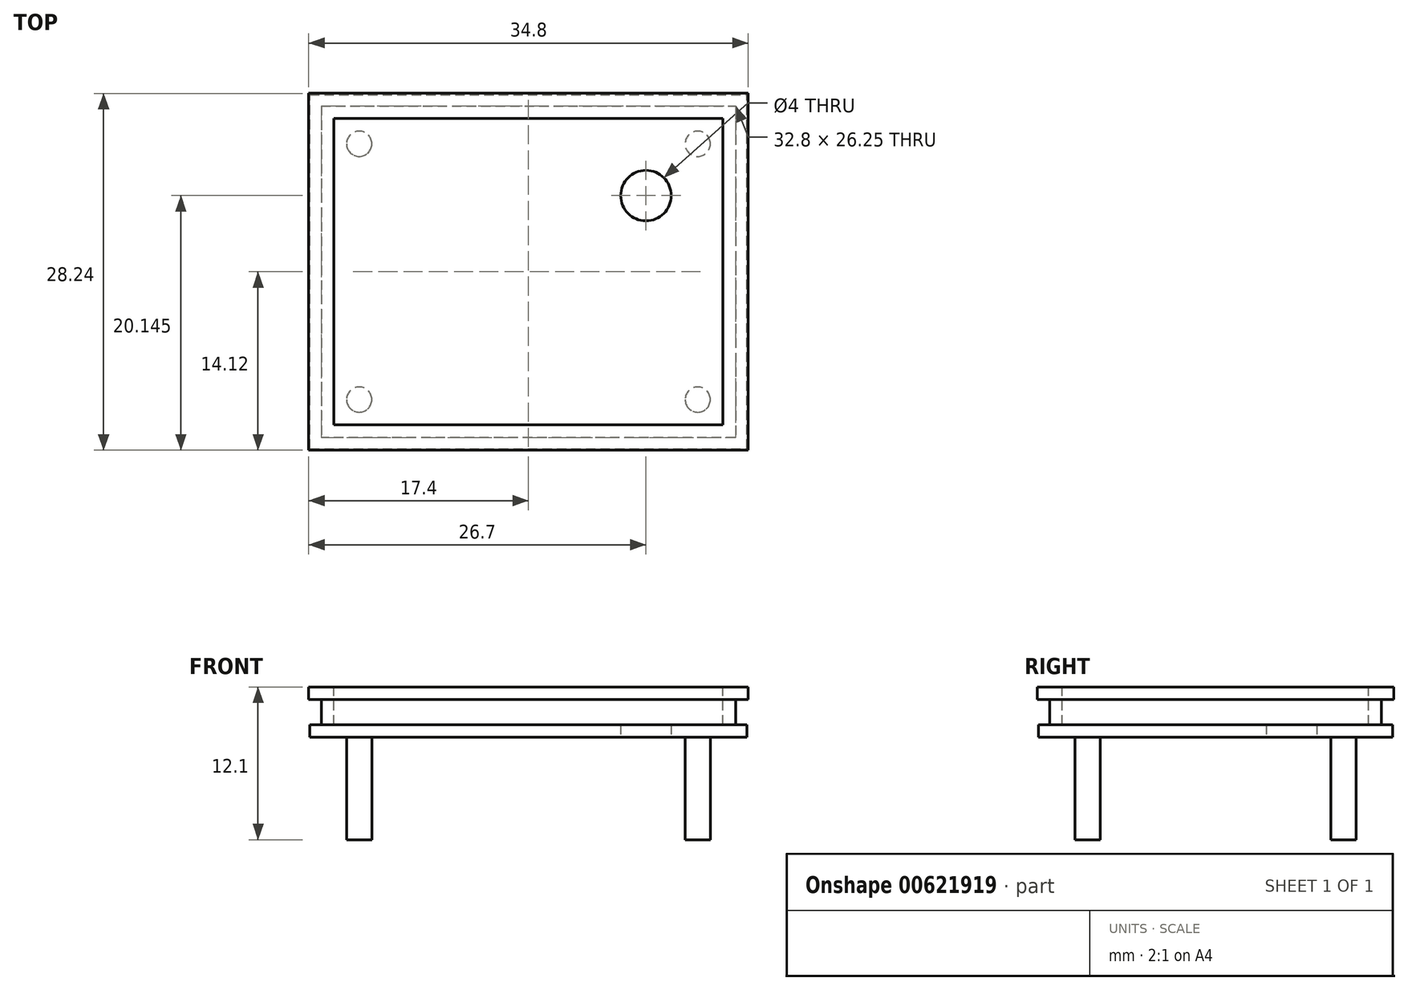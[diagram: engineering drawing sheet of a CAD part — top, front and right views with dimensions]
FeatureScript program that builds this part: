
annotation { "Feature Type Name" : "Feature", "Feature Type Description" : "" }
export const myFeature = defineFeature(function(context is Context, id is Id, definition is map)
    precondition{}
    {
        {
            var Q0;
            Q0=qCreatedBy(makeId("Top.planeOp"),FACE);
            var sketch = newSketch(context, id + "F0", { "sketchPlane" : qUnion([Q0])});
            skLineSegment(sketch, "E0.bottom", {"start": v(-17.4, -14.12) * mm, "end": v(17.4, -14.12) * mm});
            skLineSegment(sketch, "E0.top", {"start": v(-17.4, 14.13) * mm, "end": v(17.4, 14.13) * mm});
            skLineSegment(sketch, "E0.left", {"start": v(-17.4, -14.12) * mm, "end": v(-17.4, 14.13) * mm});
            skLineSegment(sketch, "E0.right", {"start": v(17.4, -14.12) * mm, "end": v(17.4, 14.13) * mm});
            skLineSegment(sketch, "E1", {"start": v(-17.4, 14.13) * mm, "end": v(17.4, -14.12) * mm});
            skLineSegment(sketch, "E2", {"start": v(17.4, 14.12) * mm, "end": v(-17.4, -14.12) * mm});
            skSolve(sketch);
        }
        {
            var Q0;
            {var subQ0=sQuery(id+"F0.wireOp",EDGE,"E0.left");Q0=makeQuery(id+"F0.imprint","IMPRINT",FACE,{"disambiguationData":[TD([[makeQuery(id+"F0.imprint","IMPRINT",EDGE,{"derivedFrom":subQ0}),-1.0]])]});}
            var Q1;
            {var subQ0=sQuery(id+"F0.wireOp",EDGE,"E0.bottom");Q1=makeQuery(id+"F0.imprint","IMPRINT",FACE,{"disambiguationData":[TD([[makeQuery(id+"F0.imprint","IMPRINT",EDGE,{"derivedFrom":subQ0}),1.0]])]});}
            var Q2;
            {var subQ0=sQuery(id+"F0.wireOp",EDGE,"E0.right");Q2=makeQuery(id+"F0.imprint","IMPRINT",FACE,{"disambiguationData":[TD([[makeQuery(id+"F0.imprint","IMPRINT",EDGE,{"derivedFrom":subQ0}),1.0]])]});}
            var Q3;
            {var subQ0=sQuery(id+"F0.wireOp",EDGE,"E0.top");Q3=makeQuery(id+"F0.imprint","IMPRINT",FACE,{"disambiguationData":[TD([[makeQuery(id+"F0.imprint","IMPRINT",EDGE,{"derivedFrom":subQ0}),-1.0]])]});}
            extrude(context, id + "F1", {"entities" : qUnion([Q0, Q1, Q2, Q3]), "depth" : 2.5 * mm, "offsetDistance" : 25 * mm});
        }
        {
            var Q0;
            Q0=makeQuery(id+"F1.opExtrude","CAP_FACE",FACE,{"disambiguationData":[OSD([sQuery(id+"F0.wireOp",EDGE,"E0.bottom"),sQuery(id+"F0.wireOp",EDGE,"E0.top"),sQuery(id+"F0.wireOp",EDGE,"E0.left"),sQuery(id+"F0.wireOp",EDGE,"E0.right")])],"isStart":false});
            var sketch = newSketch(context, id + "F2", { "sketchPlane" : qUnion([Q0])});
            skLineSegment(sketch, "E3.bottom", {"start": v(-15.4, -12.12) * mm, "end": v(15.4, -12.12) * mm});
            skLineSegment(sketch, "E3.top", {"start": v(-15.4, 12.13) * mm, "end": v(15.4, 12.13) * mm});
            skLineSegment(sketch, "E3.left", {"start": v(-15.4, -12.12) * mm, "end": v(-15.4, 12.13) * mm});
            skLineSegment(sketch, "E3.right", {"start": v(15.4, -12.12) * mm, "end": v(15.4, 12.13) * mm});
            skSolve(sketch);
        }
        {
            var Q0;
            Q0=makeQuery(id+"F2.imprint","IMPRINT",FACE,{"disambiguationData":[TD([[makeQuery(id+"F2.imprint","IMPRINT",EDGE,{"derivedFrom":sQuery(id+"F2.wireOp",EDGE,"E3.bottom")}),1.0]])]});
            extrude(context, id + "F3", {"entities" : qUnion([Q0]), "operationType" : NewBodyOperationType.REMOVE, "oppositeDirection" : true, "depth" : 1.5 * mm, "offsetDistance" : 25 * mm});
        }
        {
            var Q0;
            Q0=makeQuery(id+"F1.opExtrude","CAP_FACE",FACE,{"disambiguationData":[OSD([sQuery(id+"F0.wireOp",EDGE,"E0.bottom"),sQuery(id+"F0.wireOp",EDGE,"E0.top"),sQuery(id+"F0.wireOp",EDGE,"E0.left"),sQuery(id+"F0.wireOp",EDGE,"E0.right")])],"isStart":false});
            extrude(context, id + "F4", {"entities" : qUnion([Q0]), "operationType" : NewBodyOperationType.ADD, "depth" : 1.5 * mm, "offsetDistance" : 25 * mm});
        }
        {
            var Q0;
            {var subQ0=sQuery(id+"F0.wireOp",EDGE,"E0.bottom");Q0=makeQuery(id+"F4.boolean.opBoolean","MERGE",FACE,{"derivedFrom":[makeQuery(id+"F1.opExtrude","SWEPT_FACE",FACE,{"disambiguationData":[OSD([subQ0])]}),makeQuery(id+"F4.opExtrude","SWEPT_FACE",FACE,{"disambiguationData":[OSD([subQ0])]})]});}
            var sketch = newSketch(context, id + "F5", { "sketchPlane" : qUnion([Q0])});
            skLineSegment(sketch, "E4.bottom", {"start": v(-17.4, 3) * mm, "end": v(-16.4, 3) * mm});
            skLineSegment(sketch, "E4.top", {"start": v(-17.4, 1) * mm, "end": v(-16.4, 1) * mm});
            skLineSegment(sketch, "E4.left", {"start": v(-17.4, 3) * mm, "end": v(-17.4, 1) * mm});
            skLineSegment(sketch, "E4.right", {"start": v(-16.4, 3) * mm, "end": v(-16.4, 1) * mm});
            skSolve(sketch);
        }
        {
            var Q0;
            Q0=makeQuery(id+"F5.imprint","IMPRINT",FACE,{"disambiguationData":[TD([[makeQuery(id+"F5.imprint","IMPRINT",EDGE,{"derivedFrom":sQuery(id+"F5.wireOp",EDGE,"E4.bottom")}),-1.0]])]});
            extrude(context, id + "F6", {"entities" : qUnion([Q0]), "operationType" : NewBodyOperationType.REMOVE, "endBound" : BoundingType.THROUGH_ALL, "oppositeDirection" : true, "depth" : 25 * mm, "offsetDistance" : 25 * mm});
        }
        {
            var Q0;
            {var subQ0=sQuery(id+"F0.wireOp",EDGE,"E0.bottom");Q0=makeQuery(id+"F4.boolean.opBoolean","MERGE",FACE,{"derivedFrom":[makeQuery(id+"F1.opExtrude","SWEPT_FACE",FACE,{"disambiguationData":[OSD([subQ0])]}),makeQuery(id+"F4.opExtrude","SWEPT_FACE",FACE,{"disambiguationData":[OSD([subQ0])]})]});}
            var sketch = newSketch(context, id + "F7", { "sketchPlane" : qUnion([Q0])});
            skLineSegment(sketch, "E5.bottom", {"start": v(17.4, 3) * mm, "end": v(16.4, 3) * mm});
            skLineSegment(sketch, "E5.top", {"start": v(17.4, 1) * mm, "end": v(16.4, 1) * mm});
            skLineSegment(sketch, "E5.left", {"start": v(17.4, 3) * mm, "end": v(17.4, 1) * mm});
            skLineSegment(sketch, "E5.right", {"start": v(16.4, 3) * mm, "end": v(16.4, 1) * mm});
            skSolve(sketch);
        }
        {
            var Q0;
            Q0=makeQuery(id+"F7.imprint","IMPRINT",FACE,{"disambiguationData":[TD([[makeQuery(id+"F7.imprint","IMPRINT",EDGE,{"derivedFrom":sQuery(id+"F7.wireOp",EDGE,"E5.bottom")}),1.0]])]});
            extrude(context, id + "F8", {"entities" : qUnion([Q0]), "operationType" : NewBodyOperationType.REMOVE, "endBound" : BoundingType.THROUGH_ALL, "oppositeDirection" : true, "depth" : 25 * mm, "offsetDistance" : 25 * mm});
        }
        {
            var Q0;
            Q0=makeQuery(id+"F6.boolean.opBoolean","COPY",FACE,{"derivedFrom":makeQuery(id+"F6.opExtrude","SWEPT_FACE",FACE,{"disambiguationData":[OSD([sQuery(id+"F5.wireOp",EDGE,"E4.right")])]})});
            var sketch = newSketch(context, id + "F9", { "sketchPlane" : qUnion([Q0])});
            skLineSegment(sketch, "E6.bottom", {"start": v(13.12, 3) * mm, "end": v(14.12, 3) * mm});
            skLineSegment(sketch, "E6.top", {"start": v(13.12, 1) * mm, "end": v(14.12, 1) * mm});
            skLineSegment(sketch, "E6.left", {"start": v(13.12, 3) * mm, "end": v(13.12, 1) * mm});
            skLineSegment(sketch, "E6.right", {"start": v(14.12, 3) * mm, "end": v(14.12, 1) * mm});
            skSolve(sketch);
        }
        {
            var Q0;
            Q0=makeQuery(id+"F9.imprint","IMPRINT",FACE,{"disambiguationData":[TD([[makeQuery(id+"F9.imprint","IMPRINT",EDGE,{"derivedFrom":sQuery(id+"F9.wireOp",EDGE,"E6.bottom")}),-1.0]])]});
            extrude(context, id + "F10", {"entities" : qUnion([Q0]), "operationType" : NewBodyOperationType.REMOVE, "endBound" : BoundingType.THROUGH_ALL, "oppositeDirection" : true, "depth" : 25 * mm, "offsetDistance" : 25 * mm});
        }
        {
            var Q0;
            Q0=makeQuery(id+"F8.boolean.opBoolean","COPY",FACE,{"derivedFrom":makeQuery(id+"F8.opExtrude","SWEPT_FACE",FACE,{"disambiguationData":[OSD([sQuery(id+"F7.wireOp",EDGE,"E5.right")])]})});
            var sketch = newSketch(context, id + "F11", { "sketchPlane" : qUnion([Q0])});
            skLineSegment(sketch, "E7.bottom", {"start": v(14.13, 3) * mm, "end": v(13.13, 3) * mm});
            skLineSegment(sketch, "E7.top", {"start": v(14.13, 1) * mm, "end": v(13.13, 1) * mm});
            skLineSegment(sketch, "E7.left", {"start": v(14.13, 3) * mm, "end": v(14.13, 1) * mm});
            skLineSegment(sketch, "E7.right", {"start": v(13.13, 3) * mm, "end": v(13.13, 1) * mm});
            skSolve(sketch);
        }
        {
            var Q0;
            Q0=makeQuery(id+"F11.imprint","IMPRINT",FACE,{"disambiguationData":[TD([[makeQuery(id+"F11.imprint","IMPRINT",EDGE,{"derivedFrom":sQuery(id+"F11.wireOp",EDGE,"E7.bottom")}),1.0]])]});
            extrude(context, id + "F12", {"entities" : qUnion([Q0]), "operationType" : NewBodyOperationType.REMOVE, "endBound" : BoundingType.THROUGH_ALL, "oppositeDirection" : true, "depth" : 25 * mm, "offsetDistance" : 25 * mm});
        }
        {
            var Q0;
            Q0=makeQuery(id+"F1.opExtrude","CAP_FACE",FACE,{"disambiguationData":[OSD([sQuery(id+"F0.wireOp",EDGE,"E0.bottom"),sQuery(id+"F0.wireOp",EDGE,"E0.top"),sQuery(id+"F0.wireOp",EDGE,"E0.left"),sQuery(id+"F0.wireOp",EDGE,"E0.right")])],"isStart":true});
            var sketch = newSketch(context, id + "F13", { "sketchPlane" : qUnion([Q0])});
            skCircle(sketch, "E8", {"center": v(13.4, -10.13) * mm, "radius": 1 * mm});
            skSolve(sketch);
        }
        {
            var Q0;
            Q0=makeQuery(id+"F13.imprint","IMPRINT",FACE,{"disambiguationData":[TD([[makeQuery(id+"F13.imprint","IMPRINT",EDGE,{"derivedFrom":sQuery(id+"F13.wireOp",EDGE,"E8")}),-1.0]])]});
            var sketch = newSketch(context, id + "F14", { "sketchPlane" : qUnion([Q0])});
            skCircle(sketch, "E9", {"center": v(-13.4, -10.13) * mm, "radius": 1 * mm});
            skSolve(sketch);
        }
        {
            var Q0;
            Q0=makeQuery(id+"F14.imprint","IMPRINT",FACE,{"disambiguationData":[TD([[makeQuery(id+"F14.imprint","IMPRINT",EDGE,{"derivedFrom":sQuery(id+"F14.wireOp",EDGE,"E9")}),-1.0]])]});
            var sketch = newSketch(context, id + "F15", { "sketchPlane" : qUnion([Q0])});
            skCircle(sketch, "E10", {"center": v(-13.4, 10.12) * mm, "radius": 1 * mm});
            skSolve(sketch);
        }
        {
            var Q0;
            Q0=makeQuery(id+"F13.imprint","IMPRINT",FACE,{"disambiguationData":[TD([[makeQuery(id+"F13.imprint","IMPRINT",EDGE,{"derivedFrom":sQuery(id+"F13.wireOp",EDGE,"E8")}),-1.0]])]});
            var sketch = newSketch(context, id + "F16", { "sketchPlane" : qUnion([Q0])});
            skCircle(sketch, "E11", {"center": v(13.4, 10.12) * mm, "radius": 1 * mm});
            skSolve(sketch);
        }
        {
            var Q0;
            Q0=makeQuery(id+"F15.imprint","IMPRINT",FACE,{"disambiguationData":[TD([[makeQuery(id+"F15.imprint","IMPRINT",EDGE,{"derivedFrom":makeQuery(id+"F14.imprint","IMPRINT",EDGE,{"derivedFrom":sQuery(id+"F14.wireOp",EDGE,"E9")})}),1.0]])]});
            var Q1;
            Q1=makeQuery(id+"F13.imprint","IMPRINT",FACE,{"disambiguationData":[TD([[makeQuery(id+"F13.imprint","IMPRINT",EDGE,{"derivedFrom":sQuery(id+"F13.wireOp",EDGE,"E8")}),1.0]])]});
            var Q2;
            Q2=makeQuery(id+"F15.imprint","IMPRINT",FACE,{"disambiguationData":[TD([[makeQuery(id+"F15.imprint","IMPRINT",EDGE,{"derivedFrom":sQuery(id+"F15.wireOp",EDGE,"E10")}),1.0]])]});
            var Q3;
            Q3=makeQuery(id+"F16.imprint","IMPRINT",FACE,{"disambiguationData":[TD([[makeQuery(id+"F16.imprint","IMPRINT",EDGE,{"derivedFrom":sQuery(id+"F16.wireOp",EDGE,"E11")}),1.0]])]});
            extrude(context, id + "F17", {"entities" : qUnion([Q0, Q1, Q2, Q3]), "operationType" : NewBodyOperationType.ADD, "depth" : 8.1 * mm, "offsetDistance" : 25 * mm});
        }
        {
            var Q0;
            Q0=makeQuery(id+"F14.imprint","IMPRINT",FACE,{"disambiguationData":[TD([[makeQuery(id+"F14.imprint","IMPRINT",EDGE,{"derivedFrom":sQuery(id+"F14.wireOp",EDGE,"E9")}),-1.0]])]});
            var sketch = newSketch(context, id + "F18", { "sketchPlane" : qUnion([Q0])});
            skLineSegment(sketch, "E12.bottom", {"start": v(17.4, -14.13) * mm, "end": v(-17.4, -14.13) * mm});
            skLineSegment(sketch, "E12.top", {"start": v(17.4, 14.12) * mm, "end": v(-17.4, 14.12) * mm});
            skLineSegment(sketch, "E12.left", {"start": v(17.4, -14.13) * mm, "end": v(17.4, 14.12) * mm});
            skLineSegment(sketch, "E12.right", {"start": v(-17.4, -14.13) * mm, "end": v(-17.4, 14.12) * mm});
            skLineSegment(sketch, "E13.bottom", {"start": v(17.3, -14.03) * mm, "end": v(-17.3, -14.03) * mm});
            skLineSegment(sketch, "E13.top", {"start": v(17.3, 14.03) * mm, "end": v(-17.3, 14.02) * mm});
            skLineSegment(sketch, "E13.left", {"start": v(17.3, -14.03) * mm, "end": v(17.3, 14.03) * mm});
            skLineSegment(sketch, "E13.right", {"start": v(-17.3, -14.03) * mm, "end": v(-17.3, 14.02) * mm});
            skSolve(sketch);
        }
        {
            var Q0;
            Q0=makeQuery(id+"F18.imprint","IMPRINT",FACE,{"disambiguationData":[TD([[makeQuery(id+"F18.imprint","IMPRINT",EDGE,{"derivedFrom":sQuery(id+"F18.wireOp",EDGE,"E12.bottom")}),1.0]])]});
            var Q1;
            Q1=makeQuery(id+"F12.boolean.opBoolean","MERGE",FACE,{"derivedFrom":[makeQuery(id+"F10.boolean.opBoolean","MERGE",FACE,{"derivedFrom":[makeQuery(id+"F6.boolean.opBoolean","COPY",FACE,{"derivedFrom":makeQuery(id+"F6.opExtrude","SWEPT_FACE",FACE,{"disambiguationData":[OSD([sQuery(id+"F5.wireOp",EDGE,"E4.top")])]})}),makeQuery(id+"F8.boolean.opBoolean","COPY",FACE,{"derivedFrom":makeQuery(id+"F8.opExtrude","SWEPT_FACE",FACE,{"disambiguationData":[OSD([sQuery(id+"F7.wireOp",EDGE,"E5.top")])]})}),makeQuery(id+"F10.opExtrude","SWEPT_FACE",FACE,{"disambiguationData":[OSD([sQuery(id+"F9.wireOp",EDGE,"E6.top")])]})]}),makeQuery(id+"F12.opExtrude","SWEPT_FACE",FACE,{"disambiguationData":[OSD([sQuery(id+"F11.wireOp",EDGE,"E7.top")])]})]});
            extrude(context, id + "F19", {"entities" : qUnion([Q0]), "operationType" : NewBodyOperationType.REMOVE, "endBound" : BoundingType.UP_TO_SURFACE, "oppositeDirection" : true, "depth" : 25 * mm, "endBoundEntityFace" : qUnion([Q1]), "offsetDistance" : 25 * mm});
        }
        {
            var Q0;
            Q0=makeQuery(id+"F14.imprint","IMPRINT",FACE,{"disambiguationData":[TD([[makeQuery(id+"F14.imprint","IMPRINT",EDGE,{"derivedFrom":sQuery(id+"F14.wireOp",EDGE,"E9")}),-1.0]])]});
            var sketch = newSketch(context, id + "F20", { "sketchPlane" : qUnion([Q0])});
            skCircle(sketch, "E14", {"center": v(9.3, -6.03) * mm, "radius": 2 * mm});
            skSolve(sketch);
        }
        {
            var Q0;
            Q0=makeQuery(id+"F20.imprint","IMPRINT",FACE,{"disambiguationData":[TD([[makeQuery(id+"F20.imprint","IMPRINT",EDGE,{"derivedFrom":sQuery(id+"F20.wireOp",EDGE,"E14")}),1.0]])]});
            extrude(context, id + "F21", {"entities" : qUnion([Q0]), "operationType" : NewBodyOperationType.REMOVE, "endBound" : BoundingType.THROUGH_ALL, "oppositeDirection" : true, "depth" : 25 * mm, "offsetDistance" : 25 * mm});
        }
    });
